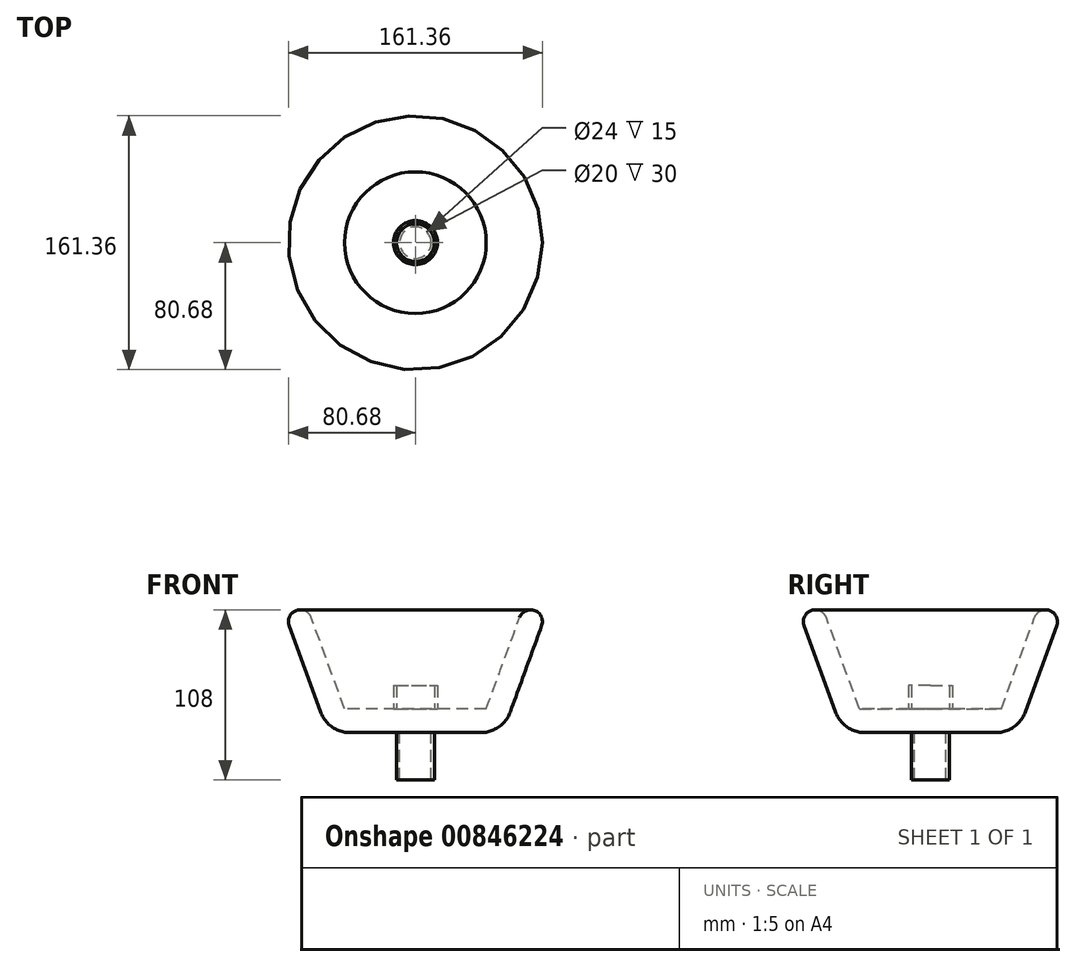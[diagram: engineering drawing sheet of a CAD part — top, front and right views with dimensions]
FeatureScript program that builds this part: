
annotation { "Feature Type Name" : "Feature", "Feature Type Description" : "" }
export const myFeature = defineFeature(function(context is Context, id is Id, definition is map)
    precondition{}
    {
        {
            var Q0;
            Q0=qCreatedBy(makeId("Front.planeOp"),FACE);
            var sketch = newSketch(context, id + "F0", { "sketchPlane" : qUnion([Q0])});
            skLineSegment(sketch, "E0", {"start": v(0, 0) * mm, "end": v(41.5, 0) * mm});
            skLineSegment(sketch, "E1", {"start": v(60.3, 13.16) * mm, "end": v(80.23, 67.93) * mm});
            skLineSegment(sketch, "E2", {"start": v(83.9, 78) * mm, "end": v(67.93, 78) * mm, "construction": true});
            skLineSegment(sketch, "E3", {"start": v(66.13, 73.07) * mm, "end": v(45, 15) * mm});
            skLineSegment(sketch, "E4", {"start": v(45, 15) * mm, "end": v(0, 15) * mm});
            skLineSegment(sketch, "E5", {"start": v(0, 15) * mm, "end": v(0, 0) * mm});
            skPoint(sketch, "E6.visualSharp", {"position": v(55.5, 0) * mm});
            skArc(sketch, "E6.filletArc", {"start": v(41.5, 0) * mm, "mid": v(52.97, 3.62) * mm, "end": v(60.3, 13.16) * mm});
            skArc(sketch, "E7", {"start": v(80.23, 67.93) * mm, "mid": v(75.75, 77.55) * mm, "end": v(66.13, 73.07) * mm});
            skSolve(sketch);
        }
        {
            var Q0;
            Q0=makeQuery(id+"F0.imprint","IMPRINT",FACE,{"disambiguationData":[TD([[makeQuery(id+"F0.imprint","IMPRINT",EDGE,{"derivedFrom":sQuery(id+"F0.wireOp",EDGE,"E0")}),1.0]])]});
            var Q1;
            Q1=sQuery(id+"F0.wireOp",EDGE,"E5");
            revolve(context, id + "F1", {"surfaceOperationType" : NewSurfaceOperationType.NEW, "entities" : qUnion([Q0]), "axis" : qUnion([Q1]), "revolveType" : RevolveType.FULL});
        }
        {
            var Q0;
            Q0=qCreatedBy(makeId("Top.planeOp"),FACE);
            var sketch = newSketch(context, id + "F2", { "sketchPlane" : qUnion([Q0])});
            skCircle(sketch, "E8", {"center": v(0, 0) * mm, "radius": 14 * mm});
            skCircle(sketch, "E9", {"center": v(0, 0) * mm, "radius": 12 * mm});
            skCircle(sketch, "E10", {"center": v(0, 0) * mm, "radius": 10 * mm});
            skSolve(sketch);
        }
        {
            var Q0;
            Q0=makeQuery(id+"F2.imprint","IMPRINT",FACE,{"disambiguationData":[TD([[makeQuery(id+"F2.imprint","IMPRINT",EDGE,{"derivedFrom":sQuery(id+"F2.wireOp",EDGE,"E8")}),1.0]])]});
            extrude(context, id + "F3", {"entities" : qUnion([Q0]), "operationType" : NewBodyOperationType.ADD, "depth" : 30 * mm, "offsetDistance" : 25 * mm});
        }
        {
            var Q0;
            Q0=makeQuery(id+"F2.imprint","IMPRINT",FACE,{"disambiguationData":[TD([[makeQuery(id+"F2.imprint","IMPRINT",EDGE,{"derivedFrom":sQuery(id+"F2.wireOp",EDGE,"E9")}),1.0]])]});
            extrude(context, id + "F4", {"entities" : qUnion([Q0]), "operationType" : NewBodyOperationType.ADD, "oppositeDirection" : true, "depth" : 30 * mm, "offsetDistance" : 25 * mm});
        }
    });
